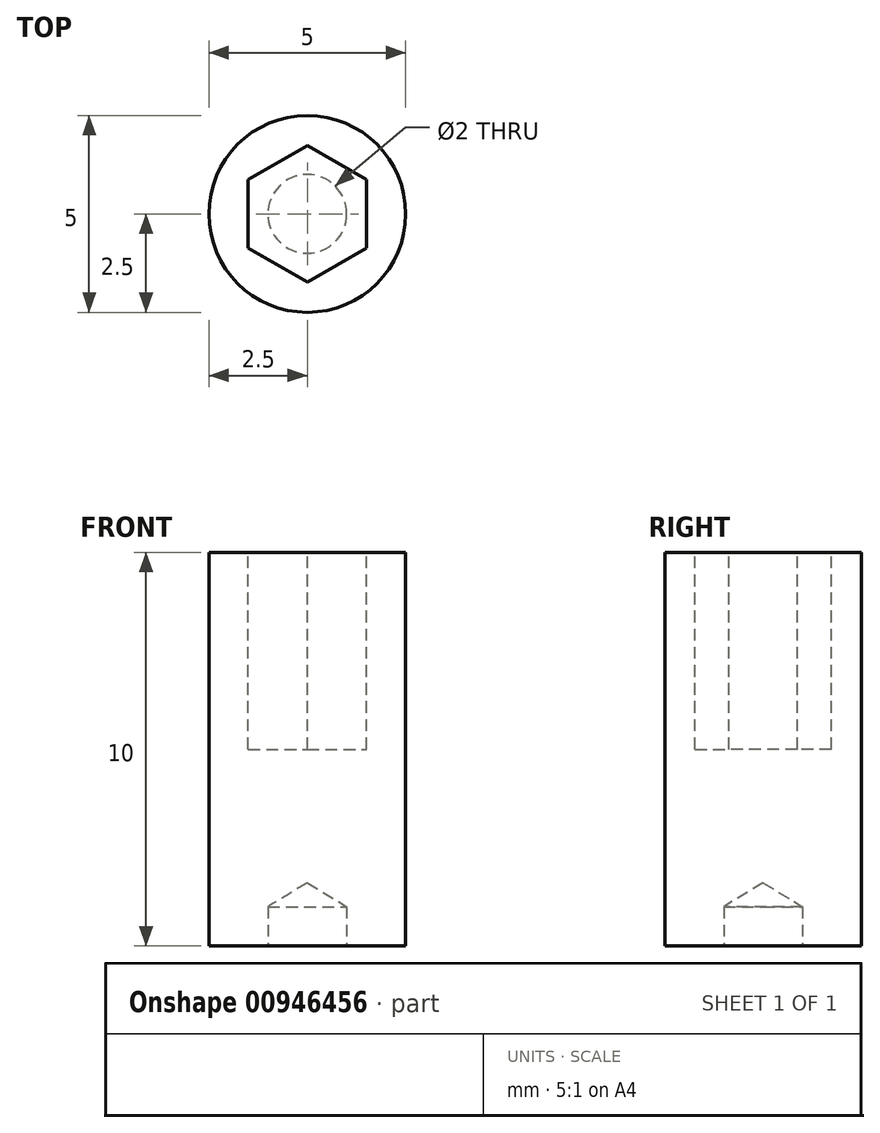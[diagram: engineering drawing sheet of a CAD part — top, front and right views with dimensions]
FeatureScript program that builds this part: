
annotation { "Feature Type Name" : "Feature", "Feature Type Description" : "" }
export const myFeature = defineFeature(function(context is Context, id is Id, definition is map)
    precondition{}
    {
        {
            var Q0;
            Q0=qCreatedBy(makeId("Top.planeOp"),FACE);
            var sketch = newSketch(context, id + "F0", { "sketchPlane" : qUnion([Q0])});
            skCircle(sketch, "E0", {"center": v(0, 0) * mm, "radius": 2.5 * mm});
            skSolve(sketch);
        }
        {
            var Q0;
            Q0 = qSketchRegion(id + "F0", true);
            extrude(context, id + "F1", {"entities" : qUnion([Q0]), "depth" : 10 * mm, "offsetDistance" : 25 * mm});
        }
        {
            var Q0;
            Q0=makeQuery(id+"F1.opExtrude","CAP_FACE",FACE,{"disambiguationData":[OSD([sQuery(id+"F0.wireOp",EDGE,"E0")])],"isStart":false});
            var sketch = newSketch(context, id + "F2", { "sketchPlane" : qUnion([Q0])});
            skCircle(sketch, "E1.cCircle", {"center": v(0, 0) * mm, "radius": 1.5 * mm, "construction": true});
            skLineSegment(sketch, "E1.0", {"start": v(1.5, 0.87) * mm, "end": v(1.5, -0.87) * mm});
            skLineSegment(sketch, "E1.1", {"start": v(1.5, -0.87) * mm, "end": v(0, -1.73) * mm});
            skLineSegment(sketch, "E1.2", {"start": v(0, -1.73) * mm, "end": v(-1.5, -0.87) * mm});
            skLineSegment(sketch, "E1.3", {"start": v(-1.5, -0.87) * mm, "end": v(-1.5, 0.87) * mm});
            skLineSegment(sketch, "E1.4", {"start": v(-1.5, 0.87) * mm, "end": v(0, 1.73) * mm});
            skLineSegment(sketch, "E1.5", {"start": v(0, 1.73) * mm, "end": v(1.5, 0.87) * mm});
            skPoint(sketch, "E1.0.midPoint", {"position": v(1.5, 0) * mm});
            skSolve(sketch);
        }
        {
            var Q0;
            Q0 = qSketchRegion(id + "F2", true);
            extrude(context, id + "F3", {"entities" : qUnion([Q0]), "operationType" : NewBodyOperationType.REMOVE, "oppositeDirection" : true, "depth" : 5 * mm, "offsetDistance" : 25 * mm});
        }
        {
            var Q0;
            Q0=makeQuery(id+"F1.opExtrude","CAP_FACE",FACE,{"disambiguationData":[OSD([sQuery(id+"F0.wireOp",EDGE,"E0")])],"isStart":true});
            var sketch = newSketch(context, id + "F4", { "sketchPlane" : qUnion([Q0])});
            skCircle(sketch, "E2", {"center": v(0, 0) * mm, "radius": 1 * mm});
            skSolve(sketch);
        }
        {
            var Q0;
            Q0=sQuery(id+"F4.wireOp",VERTEX,"E2.center");
            var Q1;
            Q1=makeQuery(id+"F1.opExtrude","SWEPT_BODY",BODY,{"disambiguationData":[OSD([sQuery(id+"F0.wireOp",EDGE,"E0")])]});
            hole(context, id + "F5", {"style" : HoleStyle.SIMPLE, "endStyle" : HoleEndStyle.BLIND, "holeDiameter" : 2 * mm, "majorDiameter" : 5 * mm, "holeDepth" : 1 * mm, "isTappedThrough" : true, "tappedDepth" : 12 * mm, "tapClearance" : 3, "locations" : qUnion([Q0]), "scope" : qUnion([Q1])});
        }
    });
